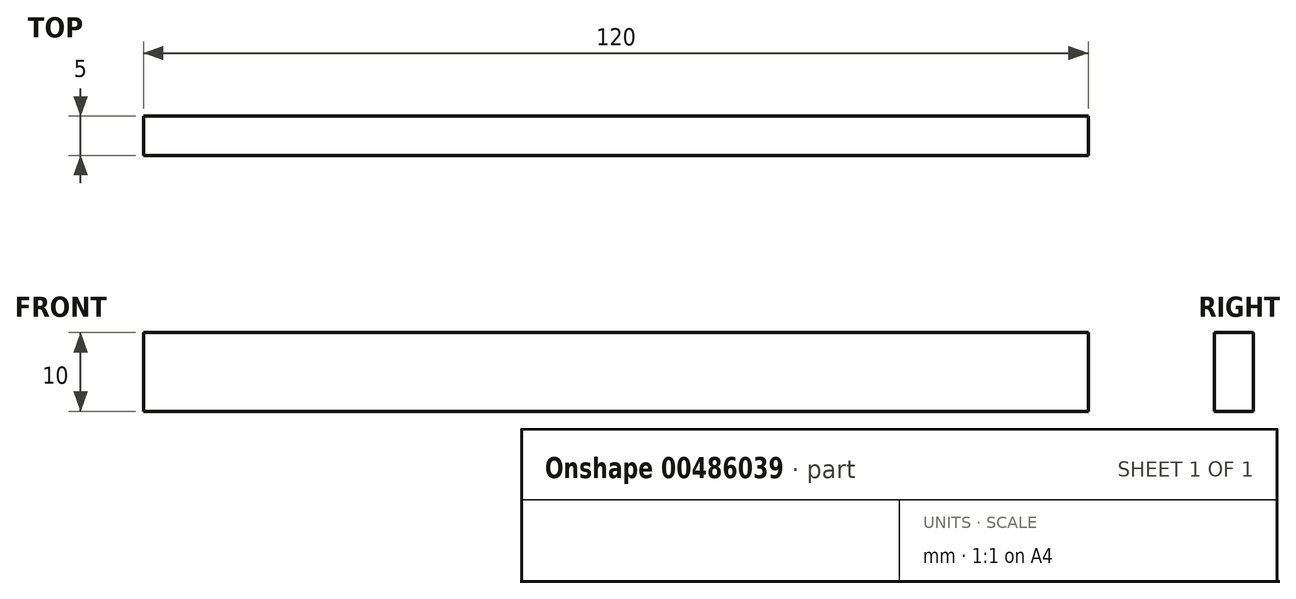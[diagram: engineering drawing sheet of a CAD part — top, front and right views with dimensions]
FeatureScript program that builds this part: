
annotation { "Feature Type Name" : "Feature", "Feature Type Description" : "" }
export const myFeature = defineFeature(function(context is Context, id is Id, definition is map)
    precondition{}
    {
        {
            var Q0;
            Q0=qCreatedBy(makeId("Front.planeOp"),FACE);
            var sketch = newSketch(context, id + "F0", { "sketchPlane" : qUnion([Q0])});
            skLineSegment(sketch, "E0.bottom", {"start": v(60, 5) * mm, "end": v(-60, 5) * mm});
            skLineSegment(sketch, "E0.top", {"start": v(60, -5) * mm, "end": v(-60, -5) * mm});
            skLineSegment(sketch, "E0.left", {"start": v(60, 5) * mm, "end": v(60, -5) * mm});
            skLineSegment(sketch, "E0.right", {"start": v(-60, 5) * mm, "end": v(-60, -5) * mm});
            skPoint(sketch, "E0.middle", {"position": v(0, 0) * mm});
            skSolve(sketch);
        }
        {
            var Q0;
            Q0=makeQuery(id+"F0.imprint","IMPRINT",FACE,{"disambiguationData":[TD([[makeQuery(id+"F0.imprint","IMPRINT",EDGE,{"derivedFrom":sQuery(id+"F0.wireOp",EDGE,"E0.bottom")}),1.0]])]});
            extrude(context, id + "F1", {"entities" : qUnion([Q0]), "depth" : 5 * mm});
        }
    });
